# Revit family: Panca VENEZIA
name_source: partatom
category: Modelli generici
revit_build: Autodesk Revit 2018 (Build: 20170223_1515(x64)
units: mm (PartAtom-declared; Revit-internal decimal feet)

## family parameters
Basato su piano di lavoro = No
Condiviso = No
Punto di calcolo locali = No
Può ospitare armatura = No
Quota connettore circolare = Usa diametro
Sempre verticale = Sì
Taglio con vuoti quando caricato = No
Tipo di parte = Normale

## types (3) — shared parameters
BIM Name = VENEZIA
BIM Object Type = SEDUTE - BENCHES
Code = 0PAPP004
Descrizione Tecnica Famiglia = "Panca lineare monolitica mod. “VENEZIA” con seduta di forma rettangolare. Panca snella con sezione trasversale a C con due appoggi per ottimizzare il peso. Abbinabile alla linea VENEZIA."
Designer = BELLITALIA DESIGN
Dimensions = 1900 mm  X 450 mm X 450 mm
Family Name = VENEZIA
Fissaggio = Appoggio
Fixings = freestanding
IFC = Furnishing Element
MASTERFORMAT 2014 (DESCRIPTION/CODE) = Benches and seat / 12 67 23
OMNICLASS (DESCRIPTION/CODE) = Exterior Benches / 23-11 29 13 11
Technical Description Family = "Monolithic linear bench mod. “VENEZIA” with seat of rectangular shape. Slim bench with C-shaped cross section with two supports to optimize weight. Can be combined with the VENEZIA line."
UNICLASS 1.4 (DESCRIPTION/CODE) = Benches / L8225
UNICLASS 2.0 (DESCRIPTION/CODE) = Chairs, Seats And Bench Seating / PR-31-12
UNIFORMAT II (DESCRIPTION/CODE) = FURNISHINGS / E20
UNSPSC CATEGORY (CODE) = 56
URL Eng = https://www.bellitalia.net
URL Ita = https://www.bellitalia.net
Weight ( kg) = 340 Kg

## per-type parameters (varying)
| type | Descrizione Tecnica per Codice | MATERIALE SEDUTA | Materiale Principale | Materiale Secondario | Primary Material | Secondary Material | Technical Description for Article |
| 0PAPP004 - GRANITO | PANCA VENEZIA IN GRANITO (COLORE A SCELTA) SABBIATO CON PIANO SUPERIORE SPAZZOLATOVERNICIATURA ANTI-DEGRADO | GRANITO | Granito Bianco | Pietre di Granito | White Granite | Reconstituted Granite | VENEZIA BENCH IN GRANITO (COLOR TO BE CHOSEN) SANDBLASTED WITH BRUSHED UPPER SURFACE ANTI-DECAY VARNISH |
| 0PAPP004 - PIETRE PREZIOSE | PANCA VENEZIA IN PIETRE PREZIOSE (COLORE A SCELTA ECCETTO VERDE ALPI) SABBIATO CON PIANO SUPERIORE SPAZZOLATOVERNICIATURA ANTI-DEGRADO | PIETRE PREZIOSE | Pietre Preziose Ricostituite Bianco Carrara | Pietre Preziose Ricostituite | Reconstituted Precious Stones - White Carrara | Reconstituted Precious Stone | VENEZIA BENCH IN PRECIOUS STONES (COLOR TO BE CHOSEN EXCEPT GREEN  ALPS) SANDBLASTED WITH BRUSHED UPPER SURFACE ANTI-DECAY VARNISH |
| 0PAPP004 - VERDE ALPI | PANCA VENEZIA IN VERDE ALPI SABBIATO CON PIANO SUPERIORE SPAZZOLATO VERNICIATURA ANTI-DEGRADO | VERDE ALPI | Pietre Preziose Ricostituite Verde Alpi | Pietre Preziose Ricostituite | Reconstituted Precious Stones - Porfido | Reconstituted Precious Stone | VENEZIA BENCH IN GREEN ALPS SANDBLASTED WITH BRUSHED UPPER  SURFACE ANTI-DECAY VARNISH |
